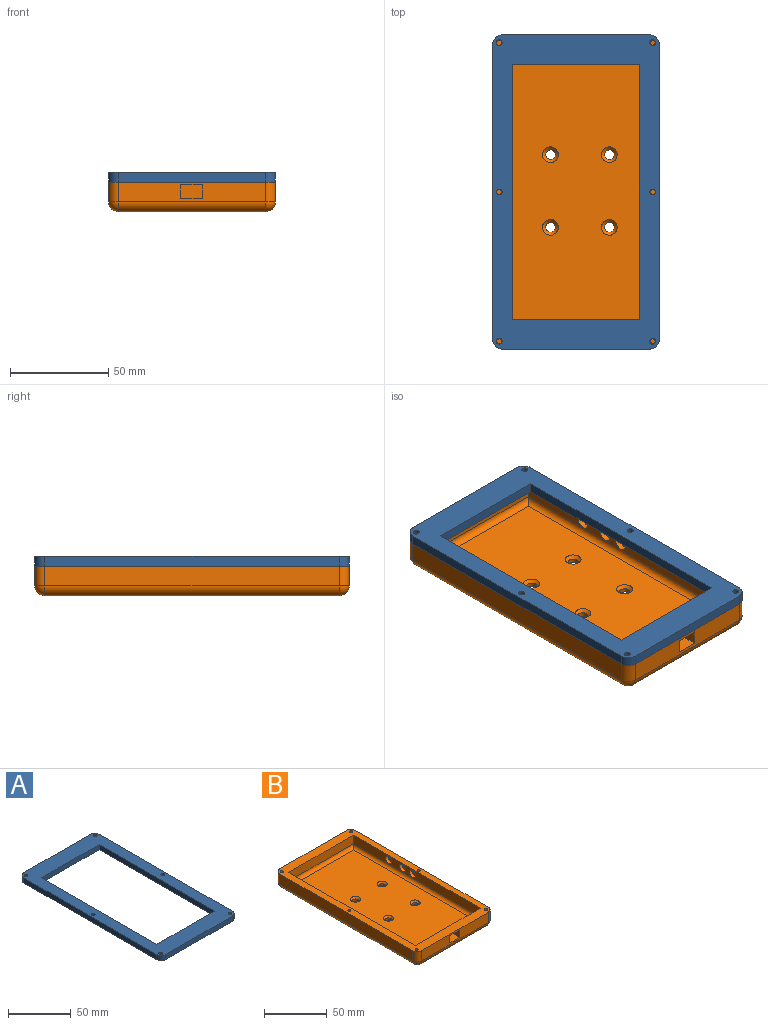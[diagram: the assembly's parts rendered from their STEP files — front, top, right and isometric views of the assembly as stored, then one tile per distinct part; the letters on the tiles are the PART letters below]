
ASSEMBLY  parts=2 mates=1
PART A: 20 faces, bbox 85x160x5 mm
  f0: plane 150x5mm, normal (-1,0,0), area 750mm2, adj f8,f9,f16,f19
  f1: plane 75x5mm, normal (0,-1,0), area 375mm2, adj f8,f9,f16,f17
  f2: plane 150x5mm, normal (1,0,0), area 750mm2, adj f8,f9,f17,f18
  f3: plane 65x5mm, normal (0,1,0), area 325mm2, adj f4,f6,f8,f9
  f4: plane 130x5mm, normal (1,0,0), area 650mm2, adj f3,f5,f8,f9
  f5: plane 65x5mm, normal (0,-1,0), area 325mm2, adj f4,f6,f8,f9
  f6: plane 130x5mm, normal (-1,0,0), area 650mm2, adj f3,f5,f8,f9
  f7: plane 75x5mm, normal (0,1,0), area 375mm2, adj f8,f9,f18,f19
  f8: plane 160x85mm, normal (0,0,1), area 5086.1mm2, adj f0,f1,f2,f3,f4,f5,f6,f7
  f9: plane 160x85mm, normal (0,0,-1), area 5086.1mm2, adj f0,f1,f2,f3,f4,f5,f6,f7
  f10: cylinder r=1.5mm len=5mm, axis (0,0,1), area 47.1mm2, adj f8,f9
  f11: cylinder r=1.5mm len=5mm, axis (0,0,1), area 47.1mm2, adj f8,f9
  f12: cylinder r=1.5mm len=5mm, axis (0,0,1), area 47.1mm2, adj f8,f9
  f13: cylinder r=1.5mm len=5mm, axis (0,0,1), area 47.1mm2, adj f8,f9
  f14: cylinder r=1.5mm len=5mm, axis (0,0,1), area 47.1mm2, adj f8,f9
  f15: cylinder r=1.5mm len=5mm, axis (0,0,1), area 47.1mm2, adj f8,f9
  f16: cylinder r=5mm len=5mm, axis (0,0,-1), area 39.3mm2, adj f0,f1,f8,f9
  f17: cylinder r=5mm len=5mm, axis (0,0,1), area 39.3mm2, adj f1,f2,f8,f9
  f18: cylinder r=5mm len=5mm, axis (0,0,-1), area 39.3mm2, adj f2,f7,f8,f9
  f19: cylinder r=5mm len=5mm, axis (0,0,1), area 39.3mm2, adj f0,f7,f8,f9
PART B: 60 faces, bbox 85x160x15 mm
  f0: plane 75x10mm, normal (0,-1,0), area 673mm2, adj f5,f25,f31,f34,f39,f40,f41,f42
  f1: plane 73x8.5mm, normal (0,1,0), area 543.5mm2, adj f5,f7,f8,f38,f39,f40,f41,f42
  f2: plane 150x10mm, normal (-1,0,0), area 1500mm2, adj f5,f28,f32,f34
  f3: plane 150x10mm, normal (1,0,0), area 1471.1mm2, adj f5,f23,f25,f26,f49,f50,f51
  f4: plane 75x10mm, normal (0,1,0), area 750mm2, adj f5,f23,f27,f28
  f5: plane 160x85mm, normal (0,0,1), area 3110.1mm2, adj f0,f1,f2,f3,f4,f7,f8,f9
  f6: plane 150x75mm, normal (0,0,-1), area 11171.5mm2, adj f26,f27,f31,f32,f52,f53,f54,f55
  f7: plane 143x8.5mm, normal (1,0,0), area 1215.5mm2, adj f1,f5,f9,f36
  f8: plane 143x8.5mm, normal (-1,0,0), area 1100mm2, adj f1,f5,f9,f37,f43,f45,f47
  f9: plane 73x8.5mm, normal (0,-1,0), area 620.5mm2, adj f5,f7,f8,f35
  f10: plane 137x67mm, normal (0,0,1), area 8977.9mm2, adj f35,f36,f37,f38,f56,f57,f58,f59
  f11: cylinder r=1.25mm len=11.5mm, axis (0,0,1), area 90.3mm2, adj f5,f12
  f12: plane 2.5x2.5mm, normal (0,0,1), area 4.9mm2, adj f11
  f13: cylinder r=1.25mm len=11.5mm, axis (0,0,1), area 90.3mm2, adj f5,f14
  f14: plane 2.5x2.5mm, normal (0,0,1), area 4.9mm2, adj f13
  f15: cylinder r=1.25mm len=11.5mm, axis (0,0,1), area 90.3mm2, adj f5,f16
  f16: plane 2.5x2.5mm, normal (0,0,1), area 4.9mm2, adj f15
  f17: cylinder r=1.25mm len=11.5mm, axis (0,0,1), area 90.3mm2, adj f5,f18
  f18: plane 2.5x2.5mm, normal (0,0,1), area 4.9mm2, adj f17
  f19: cylinder r=1.25mm len=11.5mm, axis (0,0,1), area 90.3mm2, adj f5,f20
  f20: plane 2.5x2.5mm, normal (0,0,1), area 4.9mm2, adj f19
  f21: cylinder r=1.25mm len=11.5mm, axis (0,0,1), area 90.3mm2, adj f5,f22
  f22: plane 2.5x2.5mm, normal (0,0,1), area 4.9mm2, adj f21
  f23: cylinder r=5mm len=10mm, axis (0,0,-1), area 78.5mm2, adj f3,f4,f5,f24
  f24: sphere r=5mm, area 39.3mm2, adj f23,f26,f27
  f25: cylinder r=5mm len=10mm, axis (0,0,1), area 78.5mm2, adj f0,f3,f5,f29
  f26: cylinder r=5mm len=150mm, axis (0,1,0), area 1178.1mm2, adj f3,f6,f24,f29
  f27: cylinder r=5mm len=75mm, axis (-1,0,0), area 589mm2, adj f4,f6,f24,f30
  f28: cylinder r=5mm len=10mm, axis (0,0,1), area 78.5mm2, adj f2,f4,f5,f30
  f29: sphere r=5mm, area 39.3mm2, adj f25,f26,f31
  f30: sphere r=5mm, area 39.3mm2, adj f27,f28,f32
  f31: cylinder r=5mm len=75mm, axis (1,0,0), area 589mm2, adj f0,f6,f29,f33
  f32: cylinder r=5mm len=150mm, axis (0,-1,0), area 1178.1mm2, adj f2,f6,f30,f33
  f33: sphere r=5mm, area 39.3mm2, adj f31,f32,f34
  f34: cylinder r=5mm len=10mm, axis (0,0,-1), area 78.5mm2, adj f0,f2,f5,f33
  f35: cylinder r=3mm len=73mm, axis (-1,0,0), area 333.7mm2, adj f9,f10,f36,f37
  f36: cylinder r=3mm len=143mm, axis (0,-1,0), area 663.6mm2, adj f7,f10,f35,f38
  f37: cylinder r=3mm len=143mm, axis (0,1,0), area 663.6mm2, adj f8,f10,f35,f38
  f38: cylinder r=3mm len=73mm, axis (1,0,0), area 333.7mm2, adj f1,f10,f36,f37
  f39: plane 8.5x7mm, normal (-1,0,0), area 59.5mm2, adj f0,f1,f40,f42
  f40: plane 11x8.5mm, normal (0,0,-1), area 93.5mm2, adj f0,f1,f39,f41
  f41: plane 8.5x7mm, normal (1,0,0), area 59.5mm2, adj f0,f1,f40,f42
  f42: plane 11x8.5mm, normal (0,0,1), area 93.5mm2, adj f0,f1,f39,f41
  f43: cylinder r=3.5mm len=7mm, axis (-1,0,0), area 66mm2, adj f8,f44
  f44: plane 7x7mm, normal (-1,0,0), area 28.9mm2, adj f43,f51
  f45: cylinder r=3.5mm len=7mm, axis (-1,0,0), area 66mm2, adj f8,f46
  f46: plane 7x7mm, normal (-1,0,0), area 28.9mm2, adj f45,f50
  f47: cylinder r=3.5mm len=7mm, axis (-1,0,0), area 66mm2, adj f8,f48
  f48: plane 7x7mm, normal (-1,0,0), area 28.9mm2, adj f47,f49
  f49: cylinder r=1.75mm len=3.5mm, axis (1,0,0), area 27.5mm2, adj f3,f48
  f50: cylinder r=1.75mm len=3.5mm, axis (1,0,0), area 27.5mm2, adj f3,f46
  f51: cylinder r=1.75mm len=3.5mm, axis (1,0,0), area 27.5mm2, adj f3,f44
  f52: cylinder r=2.5mm len=5mm, axis (0,0,1), area 31.4mm2, adj f6,f58
  f53: cylinder r=2.5mm len=5mm, axis (0,0,1), area 31.4mm2, adj f6,f57
  f54: cylinder r=2.5mm len=5mm, axis (0,0,1), area 31.4mm2, adj f6,f56
  f55: cylinder r=2.5mm len=5mm, axis (0,0,1), area 31.4mm2, adj f6,f59
  f56: cone r=2.5mm half-angle=45deg, axis (0,0,1), area 43.3mm2, adj f10,f54
  f57: cone r=2.5mm half-angle=45deg, axis (0,0,1), area 43.3mm2, adj f10,f53
  f58: cone r=2.5mm half-angle=45deg, axis (0,0,1), area 43.3mm2, adj f10,f52
  f59: cone r=2.5mm half-angle=45deg, axis (0,0,1), area 43.3mm2, adj f10,f55
PLACE A t=(-44.27,51.48,-9.77)mm
PLACE B t=(-44.27,51.48,-24.77)mm
MATE fastened A.f14 <-> B.f15  axis (0,0,-1) through (-4.9,-104.52,-9.77)mm
